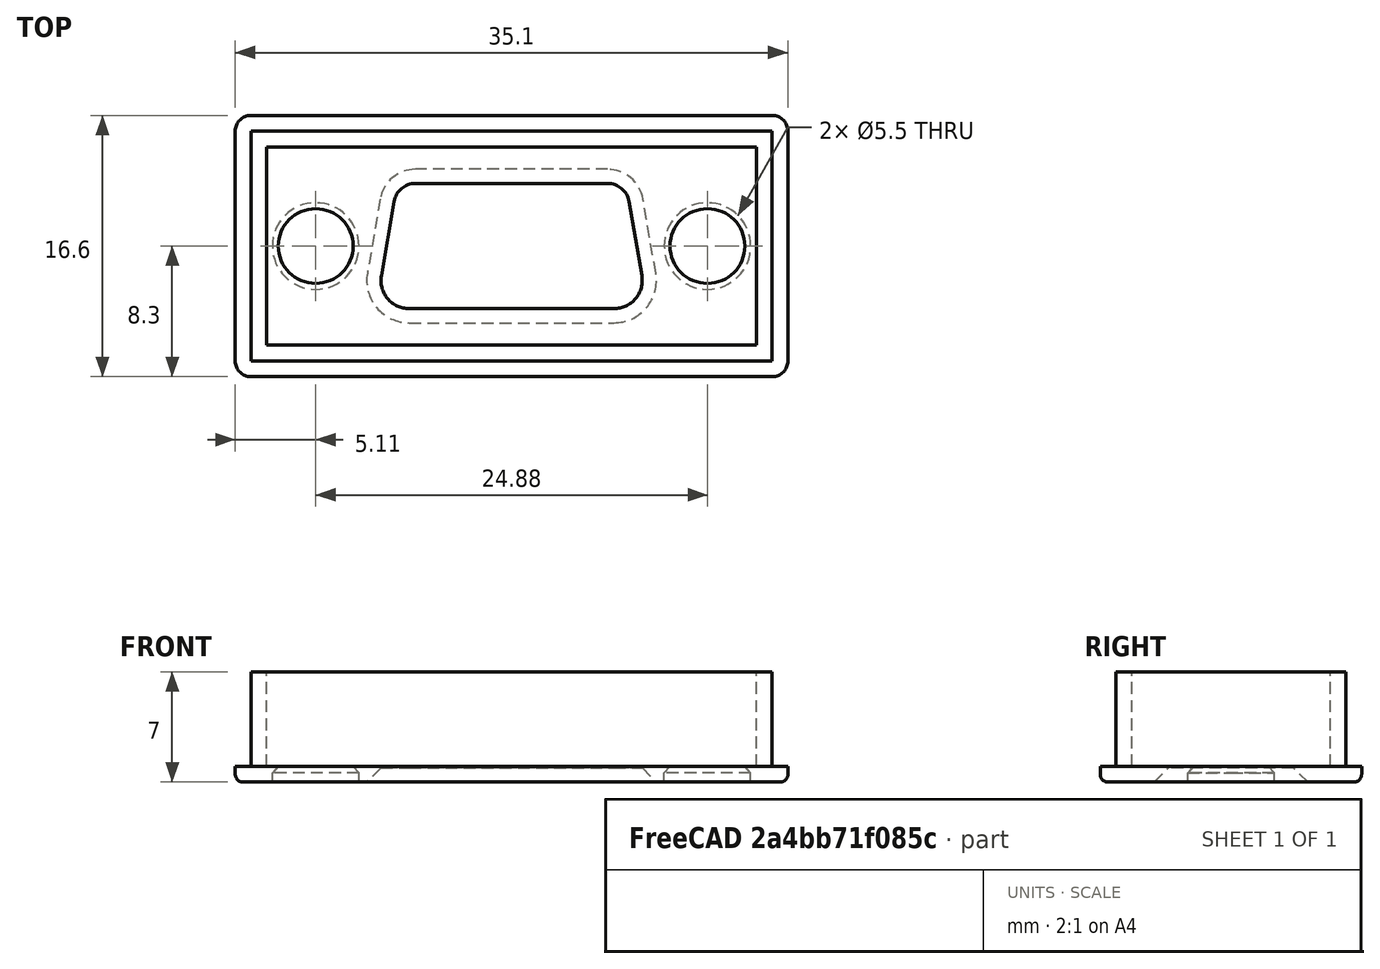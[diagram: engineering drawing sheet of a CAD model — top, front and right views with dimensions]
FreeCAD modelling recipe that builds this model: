
FCSTD DOCUMENT  (FreeCAD 0.18R13728 (Git))
Label: test115_vgachanger
License: All rights reserved
LicenseURL: http://en.wikipedia.org/wiki/All_rights_reserved
objects: Sketcher::SketchObject×3, PartDesign::Pad×2, PartDesign::Fillet×1, PartDesign::Chamfer×1, PartDesign::Plane×1, PartDesign::SubtractivePipe×1, PartDesign::LinearPattern×1, PartDesign::Body×1, Mesh::Feature×1
note: 14 computed .brp shape members not serialized (recipe doc carries the construction recipe); baked Part::Feature solids carry a one-line shape summary decoded from their .brp

FEATURE [Sketcher::SketchObject] Sketch
  MapMode = 5
  Support = -> [XY_Plane]
  sketch-geometry (8):
    g0: LineSegment StartX=-15.55 StartY=-6.3 StartZ=0 EndX=15.55 EndY=-6.3 EndZ=0
    g1: LineSegment StartX=15.55 StartY=-6.3 StartZ=0 EndX=15.55 EndY=6.3 EndZ=0
    g2: LineSegment StartX=15.55 StartY=6.3 StartZ=0 EndX=-15.55 EndY=6.3 EndZ=0
    g3: LineSegment StartX=-15.55 StartY=6.3 StartZ=0 EndX=-15.55 EndY=-6.3 EndZ=0
    g4: LineSegment StartX=-16.55 StartY=7.3 StartZ=0 EndX=16.55 EndY=7.3 EndZ=0
    g5: LineSegment StartX=16.55 StartY=7.3 StartZ=0 EndX=16.55 EndY=-7.3 EndZ=0
    g6: LineSegment StartX=16.55 StartY=-7.3 StartZ=0 EndX=-16.55 EndY=-7.3 EndZ=0
    g7: LineSegment StartX=-16.55 StartY=-7.3 StartZ=0 EndX=-16.55 EndY=7.3 EndZ=0
  constraints (22):
    c: Coincident(g0,g1)
    c: Coincident(g1,g2)
    c: Coincident(g2,g3)
    c: Coincident(g3,g0)
    c: Horizontal(g0)
    c: Horizontal(g2)
    c: Vertical(g1)
    c: Vertical(g3)
    c: Symmetric(g2,g0,g-1)
    c: Distance(g2) = 31.1
    c: Distance(g1) = 12.6
    c: Coincident(g4,g5)
    c: Coincident(g5,g6)
    c: Coincident(g6,g7)
    c: Coincident(g7,g4)
    c: Horizontal(g4)
    c: Horizontal(g6)
    c: Vertical(g5)
    c: Vertical(g7)
    c: Symmetric(g7,g5,g-1)
    c: Distance(g2,g4) = 1
    c: Distance(g2,g7) = 1
FEATURE [PartDesign::Pad] Pad
  Length = 6
  Length2 = 100
  Profile = -> Sketch
  Type = 0
FEATURE [Sketcher::SketchObject] Sketch001
  ExternalGeometry = -> [Pad]
  MapMode = 5
  Placement = pos=(0,0,0) rot=(1,0,0;3.14159rad)
  Support = -> [Pad]
  sketch-geometry (24):
    g0: LineSegment [constr] StartX=-8.3 StartY=3.975 StartZ=0 EndX=8.3 EndY=3.975 EndZ=0
    g1: LineSegment [constr] StartX=8.3 StartY=3.975 StartZ=0 EndX=8.3 EndY=-3.975 EndZ=0
    g2: LineSegment [constr] StartX=8.3 StartY=-3.975 StartZ=0 EndX=-8.3 EndY=-3.975 EndZ=0
    g3: LineSegment [constr] StartX=-8.3 StartY=-3.975 StartZ=0 EndX=-8.3 EndY=3.975 EndZ=0
    g4: LineSegment StartX=-6.1 StartY=-3.975 StartZ=0 EndX=6.1 EndY=-3.975 EndZ=0
    g5: LineSegment StartX=-6.5 StartY=3.975 StartZ=0 EndX=6.5 EndY=3.975 EndZ=0
    g6: ArcOfCircle CenterX=-6.09999 CenterY=-2.59515 CenterZ=0 NormalX=0 NormalY=0 NormalZ=1 AngleXU=0 Radius=1.37985 StartAngle=3.31314 EndAngle=4.71238
    g7: ArcOfCircle CenterX=-6.5 CenterY=2.175 CenterZ=0 NormalX=0 NormalY=0 NormalZ=1 AngleXU=0 Radius=1.8 StartAngle=1.5708 EndAngle=3.31314
    g8: ArcOfCircle CenterX=6.5 CenterY=2.175 CenterZ=0 NormalX=0 NormalY=0 NormalZ=1 AngleXU=0 Radius=1.8 StartAngle=6.11164 EndAngle=7.85398
    g9: ArcOfCircle CenterX=6.09999 CenterY=-2.59515 CenterZ=0 NormalX=0 NormalY=0 NormalZ=1 AngleXU=0 Radius=1.37985 StartAngle=4.71239 EndAngle=6.11164
    g10: LineSegment StartX=7.45959 StartY=-2.8307 StartZ=0 EndX=8.27358 EndY=1.86773 EndZ=0
    g11: LineSegment StartX=-7.45959 StartY=-2.8307 StartZ=0 EndX=-8.27358 EndY=1.86773 EndZ=0
    g12: Circle CenterX=-12.44 CenterY=0 CenterZ=0 NormalX=0 NormalY=0 NormalZ=1 AngleXU=0 Radius=2.375
    g13: Circle CenterX=12.44 CenterY=0 CenterZ=0 NormalX=0 NormalY=0 NormalZ=1 AngleXU=0 Radius=2.375
    g14: LineSegment StartX=-16.55 StartY=8.3 StartZ=0 EndX=16.55 EndY=8.3 EndZ=0
    g15: LineSegment StartX=17.55 StartY=7.3 StartZ=0 EndX=17.55 EndY=-7.3 EndZ=0
    g16: LineSegment StartX=16.55 StartY=-8.3 StartZ=0 EndX=-16.55 EndY=-8.3 EndZ=0
    g17: LineSegment StartX=-17.55 StartY=-7.3 StartZ=0 EndX=-17.55 EndY=7.3 EndZ=0
    g18: ArcOfCircle CenterX=-16.55 CenterY=7.3 CenterZ=0 NormalX=0 NormalY=0 NormalZ=1 AngleXU=0 Radius=1 StartAngle=1.5708 EndAngle=3.14159
    g19: ArcOfCircle CenterX=16.55 CenterY=7.3 CenterZ=0 NormalX=0 NormalY=0 NormalZ=1 AngleXU=0 Radius=1 StartAngle=0 EndAngle=1.5708
    g20: ArcOfCircle CenterX=16.55 CenterY=-7.3 CenterZ=0 NormalX=0 NormalY=0 NormalZ=1 AngleXU=0 Radius=1 StartAngle=4.71239 EndAngle=6.28319
    g21: ArcOfCircle CenterX=-16.55 CenterY=-7.3 CenterZ=0 NormalX=0 NormalY=0 NormalZ=1 AngleXU=0 Radius=1 StartAngle=3.14159 EndAngle=4.71239
    g22: GeomPoint X=-7.95 Y=0 Z=0
    g23: GeomPoint X=7.95 Y=0 Z=0
  constraints (66):
    c: Coincident(g0,g1)
    c: Coincident(g1,g2)
    c: Coincident(g2,g3)
    c: Coincident(g3,g0)
    c: Vertical(g1)
    c: Vertical(g3)
    c: Distance(g0) = 16.6
    c: Distance(g1) = 7.95
    c: PointOnObject(g4,g2)
    c: PointOnObject(g4,g2)
    c: PointOnObject(g5,g0)
    c: PointOnObject(g5,g0)
    c: Coincident(g6,g4)
    c: Coincident(g7,g5)
    c: Coincident(g8,g5)
    c: Coincident(g9,g4)
    c: Coincident(g10,g9)
    c: Coincident(g10,g8)
    c: Coincident(g11,g7)
    c: Coincident(g11,g6)
    c: Tangent(g11,g6)
    c: Tangent(g7,g11)
    c: Tangent(g9,g10)
    c: Tangent(g8,g10)
    c: Symmetric(g4,g4,g-2)
    c: Symmetric(g5,g5,g-2)
    c: Tangent(g6,g4)
    c: Tangent(g8,g5)
    c: Tangent(g7,g5)
    c: Tangent(g4,g9)
    c: Tangent(g7,g3)
    c: Tangent(g8,g1)
    c: Radius(g7) = 1.8
    c: Equal(g7,g8)
    c: Symmetric(g1,g0,g-1)
    c: PointOnObject(g12,g-1)
    c: Radius(g12) = 2.375
    c: Equal(g12,g13)
    c: Distance(g12,g-4) = 3.11
    c: Symmetric(g12,g13,g-2)
    c: Horizontal(g14)
    c: Horizontal(g16)
    c: Vertical(g15)
    c: Vertical(g17)
    c: Distance(g-6,g14) = 1
    c: Distance(g-6,g17) = 1
    c: Tangent(g17,g18) = 1.5708
    c: Tangent(g14,g18) = 1.5708
    c: Tangent(g14,g19) = 1.5708
    c: Tangent(g15,g19) = 1.5708
    c: Tangent(g16,g20) = 1.5708
    c: Tangent(g15,g20) = 1.5708
    c: Tangent(g16,g21) = 1.5708
    c: Tangent(g17,g21) = 1.5708
    c: Radius(g18) = 1
    c: Equal(g18,g19)
    c: Equal(g18,g20)
    c: Equal(g18,g21)
    c: Symmetric(g18,g20,g-1)
    c: PointOnObject(g22,g11)
    c: PointOnObject(g23,g10)
    c: PointOnObject(g23,g-1)
    c: PointOnObject(g22,g-1)
    c: Distance(g22,g23) = 15.9
    c: Symmetric(g6,g9,g-2)
    c: Distance(g4) = 12.2
FEATURE [PartDesign::Pad] Pad001
  BaseFeature = -> Pad
  Length = 1
  Length2 = 100
  Profile = -> Sketch001
  Type = 0
FEATURE [PartDesign::Fillet] Fillet
  Base = -> Pad001 [Edge53]
  BaseFeature = -> Pad001
  Radius = 0.5
FEATURE [PartDesign::Chamfer] Chamfer
  Base = -> Fillet [Edge38]
  BaseFeature = -> Fillet
  Size = 0.9
FEATURE [PartDesign::Plane] DatumPlane
  AttachmentOffset = pos=(0,0,0) rot=(-1,0,0;1.5708rad)
  MapMode = 7
  Placement = pos=(-10.065,0,0) rot=(-1,0,0;1.5708rad)
  Support = -> [Chamfer]
FEATURE [Sketcher::SketchObject] Sketch003
  ExternalGeometry = -> [Chamfer]
  MapMode = 5
  Placement = pos=(-10.065,0,0) rot=(-1,0,0;1.5708rad)
  Support = -> [DatumPlane]
  sketch-geometry (5):
    g0: LineSegment StartX=0 StartY=1 StartZ=0 EndX=0.375 EndY=1 EndZ=0
    g1: LineSegment StartX=0.375 StartY=1 StartZ=0 EndX=0.375 EndY=0.4 EndZ=0
    g2: LineSegment StartX=0.375 StartY=0.4 StartZ=0 EndX=0 EndY=0 EndZ=0
    g3: LineSegment StartX=0 StartY=0 StartZ=0 EndX=0 EndY=1 EndZ=0
    g4: LineSegment [constr] StartX=0 StartY=1 StartZ=0 EndX=-2.375 EndY=1 EndZ=0
  constraints (13):
    c: Coincident(g0,g1)
    c: Coincident(g1,g2)
    c: Coincident(g2,g3)
    c: Coincident(g3,g0)
    c: Horizontal(g0)
    c: Vertical(g1)
    c: Coincident(g0,g-3)
    c: Coincident(g-1,g2)
    c: Coincident(g4,g0)
    c: Horizontal(g4)
    c: Distance(g4) = 2.375
    c: Distance(g1,g-1) = 0.4
    c: DistanceX(g4,g0) = 2.75
FEATURE [PartDesign::SubtractivePipe] SubtractivePipe
  AuxilleryCurvelinear = true
  AuxillerySpineTangent = false
  BaseFeature = -> Chamfer
  Binormal = (0,0,0)
  Mode = 0
  Profile = -> Sketch003
  Spine = -> Chamfer [Edge18]
  SpineTangent = false
  Transformation = 0
  Transition = 0
FEATURE [PartDesign::LinearPattern] LinearPattern  label="DontDoThisWay"
  BaseFeature = -> SubtractivePipe
  Direction = -> Sketch003 [H_Axis]
  Length = 24.88
  Occurrences = 2
  Originals = -> [SubtractivePipe]
FEATURE [PartDesign::Body] Body
  Group = -> [Sketch,Pad,Sketch001,Pad001,Fillet,Chamfer,DatumPlane,Sketch003,SubtractivePipe,LinearPattern]
  Origin = -> Origin
  Tip = -> LinearPattern
FEATURE [Mesh::Feature] Mesh  label="DontDoThisWay (Meshed)"
